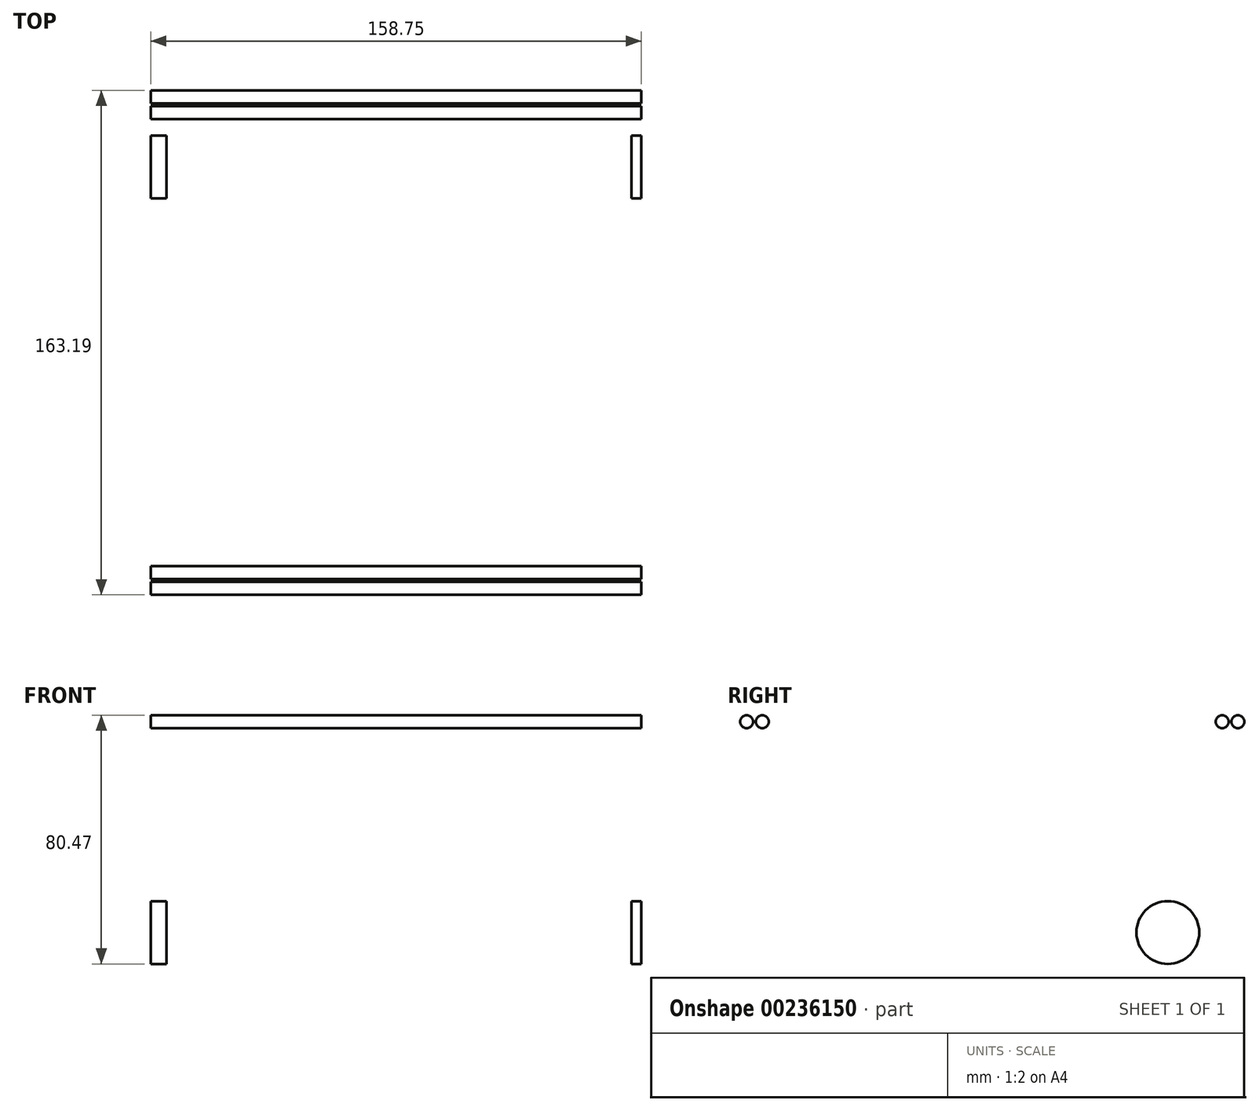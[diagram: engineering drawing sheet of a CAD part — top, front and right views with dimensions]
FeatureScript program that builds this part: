
annotation { "Feature Type Name" : "Feature", "Feature Type Description" : "" }
export const myFeature = defineFeature(function(context is Context, id is Id, definition is map)
    precondition{}
    {
        {
            var Q0;
            Q0=qCreatedBy(makeId("Top.planeOp"),FACE);
            var sketch = newSketch(context, id + "F0", { "sketchPlane" : qUnion([Q0])});
            skLineSegment(sketch, "E0.bottom", {"start": v(-87.64, 54.23) * mm, "end": v(71.1, 54.23) * mm});
            skLineSegment(sketch, "E0.top", {"start": v(-87.64, -104.78) * mm, "end": v(71.1, -104.78) * mm});
            skLineSegment(sketch, "E0.left", {"start": v(-87.64, 54.23) * mm, "end": v(-87.64, -104.78) * mm});
            skLineSegment(sketch, "E0.right", {"start": v(71.1, 54.23) * mm, "end": v(71.1, -104.78) * mm});
            skLineSegment(sketch, "E1.bottom", {"start": v(-94, 54.23) * mm, "end": v(-87.64, 54.23) * mm});
            skLineSegment(sketch, "E1.top", {"start": v(-94, 47.62) * mm, "end": v(-87.64, 47.62) * mm});
            skLineSegment(sketch, "E1.left", {"start": v(-94, 54.23) * mm, "end": v(-94, 47.63) * mm});
            skLineSegment(sketch, "E1.right", {"start": v(-87.64, 54.23) * mm, "end": v(-87.64, 47.63) * mm});
            skLineSegment(sketch, "E2", {"start": v(-91.77, 0) * mm, "end": v(128.93, 0) * mm, "construction": true});
            skLineSegment(sketch, "E3.bottom", {"start": v(-82.56, 49.15) * mm, "end": v(67.93, 49.15) * mm});
            skLineSegment(sketch, "E3.top", {"start": v(-82.56, -99.7) * mm, "end": v(67.93, -99.7) * mm});
            skLineSegment(sketch, "E3.left", {"start": v(-82.56, 49.15) * mm, "end": v(-82.56, -99.7) * mm});
            skLineSegment(sketch, "E3.right", {"start": v(67.93, 49.15) * mm, "end": v(67.93, -99.7) * mm});
            skLineSegment(sketch, "E4.0.1.0", {"start": v(-94, -3.18) * mm, "end": v(-87.64, -3.18) * mm});
            skLineSegment(sketch, "E4.0.1.1", {"start": v(-94, 3.43) * mm, "end": v(-94, -3.17) * mm});
            skLineSegment(sketch, "E4.0.1.2", {"start": v(-94, 3.43) * mm, "end": v(-87.64, 3.43) * mm});
            skLineSegment(sketch, "E4.0.2.0", {"start": v(-94, -53.98) * mm, "end": v(-87.64, -53.98) * mm});
            skLineSegment(sketch, "E4.0.2.1", {"start": v(-94, -47.37) * mm, "end": v(-94, -53.98) * mm});
            skLineSegment(sketch, "E4.0.2.2", {"start": v(-94, -47.37) * mm, "end": v(-87.64, -47.37) * mm});
            skLineSegment(sketch, "E4.0.3.0", {"start": v(-94, -104.78) * mm, "end": v(-87.64, -104.78) * mm});
            skLineSegment(sketch, "E4.0.3.1", {"start": v(-94, -98.17) * mm, "end": v(-94, -104.78) * mm});
            skLineSegment(sketch, "E4.0.3.2", {"start": v(-94, -98.17) * mm, "end": v(-87.64, -98.17) * mm});
            skLineSegment(sketch, "E4.direction1", {"start": v(-94, 47.63) * mm, "end": v(-68.6, 47.63) * mm, "construction": true});
            skLineSegment(sketch, "E4.direction2", {"start": v(-94, 47.63) * mm, "end": v(-94, -3.17) * mm, "construction": true});
            skSolve(sketch);
        }
        {
            var Q0;
            Q0=makeQuery(id+"F0.imprint","IMPRINT",FACE,{"disambiguationData":[TD([[makeQuery(id+"F0.imprint","IMPRINT",EDGE,{"derivedFrom":sQuery(id+"F0.wireOp",EDGE,"E0.bottom")}),-1.0]])]});
            var Q1;
            Q1=makeQuery(id+"F0.imprint","IMPRINT",FACE,{"disambiguationData":[TD([[makeQuery(id+"F0.imprint","IMPRINT",EDGE,{"derivedFrom":sQuery(id+"F0.wireOp",EDGE,"E1.bottom")}),-1.0]])]});
            var Q2;
            {var subQ0=sQuery(id+"F0.wireOp",EDGE,"E4.0.1.0");Q2=makeQuery(id+"F0.imprint","IMPRINT",FACE,{"disambiguationData":[TD([[makeQuery(id+"F0.imprint","IMPRINT",EDGE,{"derivedFrom":subQ0}),1.0]])]});}
            var Q3;
            {var subQ0=sQuery(id+"F0.wireOp",EDGE,"E4.0.2.0");Q3=makeQuery(id+"F0.imprint","IMPRINT",FACE,{"disambiguationData":[TD([[makeQuery(id+"F0.imprint","IMPRINT",EDGE,{"derivedFrom":subQ0}),1.0]])]});}
            var Q4;
            {var subQ0=sQuery(id+"F0.wireOp",EDGE,"E4.0.3.0");Q4=makeQuery(id+"F0.imprint","IMPRINT",FACE,{"disambiguationData":[TD([[makeQuery(id+"F0.imprint","IMPRINT",EDGE,{"derivedFrom":subQ0}),1.0]])]});}
            extrude(context, id + "F1", {"entities" : qUnion([Q0, Q1, Q2, Q3, Q4]), "depth" : 88.9 * mm});
        }
        {
            var Q0;
            {var subQ0=sQuery(id+"F0.wireOp",EDGE,"E0.left");Q0=makeQuery(id+"F1.opExtrude","SWEPT_FACE",FACE,{"disambiguationData":[OSD([subQ0]),TDD([makeQuery(id+"F0.imprint","IMPRINT",EDGE,{"disambiguationData":[TD([[makeQuery(id+"F0.imprint","INTERSECT",VERTEX,{"derivedFrom":[subQ0,sQuery(id+"F0.wireOp",EDGE,"E4.0.1.2")]}),1.0]])],"derivedFrom":subQ0})])]});}
            var sketch = newSketch(context, id + "F2", { "sketchPlane" : qUnion([Q0])});
            skCircle(sketch, "E5", {"center": v(-49.15, 86.8) * mm, "radius": 2.1 * mm});
            skCircle(sketch, "E6", {"center": v(99.7, 86.8) * mm, "radius": 2.1 * mm});
            skCircle(sketch, "E7", {"center": v(104.78, 86.8) * mm, "radius": 2.1 * mm});
            skCircle(sketch, "E8", {"center": v(-54.23, 86.8) * mm, "radius": 2.1 * mm});
            skSolve(sketch);
        }
        {
            var Q0;
            Q0=makeQuery(id+"F1.opExtrude","SWEPT_FACE",FACE,{"disambiguationData":[OSD([sQuery(id+"F0.wireOp",EDGE,"E0.right")])]});
            var sketch = newSketch(context, id + "F3", { "sketchPlane" : qUnion([Q0])});
            skCircle(sketch, "E9", {"center": v(-25.27, 88.9) * mm, "radius": 74.36 * mm});
            skPoint(sketch, "E9.first.point", {"position": v(-99.63, 88.9) * mm});
            skPoint(sketch, "E9.third.point", {"position": v(49.08, 88.9) * mm});
            skCircle(sketch, "E10", {"center": v(-82.12, 18.59) * mm, "radius": 10.16 * mm});
            skLineSegment(sketch, "E11", {"start": v(-25.27, 0) * mm, "end": v(-25.27, 125.52) * mm, "construction": true});
            skCircle(sketch, "E12.MirrorC", {"center": v(31.57, 18.59) * mm, "radius": 10.16 * mm});
            skSolve(sketch);
        }
        {
            var Q0;
            {var subQ0=sQuery(id+"F3.wireOp",EDGE,"E9");var subQ1=makeQuery(id+"F1.opExtrude","CAP_EDGE",EDGE,{"disambiguationData":[OSD([sQuery(id+"F0.wireOp",EDGE,"E0.right")])],"isStart":false});var subQ2=makeQuery(id+"F3.imprint","INTERSECT",VERTEX,{"disambiguationData":[OD(0.0)],"derivedFrom":[subQ1,subQ0]});Q0=makeQuery(id+"F3.imprint","IMPRINT",FACE,{"disambiguationData":[TD([[makeQuery(id+"F3.imprint","IMPRINT",EDGE,{"disambiguationData":[TD([[subQ2,1.0]])],"derivedFrom":subQ0}),1.0]])]});}
            var Q1;
            Q1=makeQuery(id+"F3.imprint","IMPRINT",FACE,{"disambiguationData":[TD([[makeQuery(id+"F3.imprint","IMPRINT",EDGE,{"derivedFrom":sQuery(id+"F3.wireOp",EDGE,"E10")}),1.0]])]});
            var Q2;
            Q2=makeQuery(id+"F3.imprint","IMPRINT",FACE,{"disambiguationData":[TD([[makeQuery(id+"F3.imprint","IMPRINT",EDGE,{"derivedFrom":sQuery(id+"F3.wireOp",EDGE,"E12.MirrorC")}),-1.0]])]});
            extrude(context, id + "F4", {"entities" : qUnion([Q0, Q1, Q2]), "operationType" : NewBodyOperationType.REMOVE, "oppositeDirection" : true, "depth" : 187.7 * mm});
        }
        {
            var Q0;
            Q0=makeQuery(id+"F2.imprint","IMPRINT",FACE,{"disambiguationData":[TD([[makeQuery(id+"F2.imprint","IMPRINT",EDGE,{"derivedFrom":sQuery(id+"F2.wireOp",EDGE,"E7")}),1.0]])]});
            var Q1;
            Q1=makeQuery(id+"F2.imprint","IMPRINT",FACE,{"disambiguationData":[TD([[makeQuery(id+"F2.imprint","IMPRINT",EDGE,{"derivedFrom":sQuery(id+"F2.wireOp",EDGE,"E8")}),1.0]])]});
            var Q2;
            {var subQ0=sQuery(id+"F2.wireOp",EDGE,"E5");var subQ1=makeQuery(id+"F1.opExtrude","SWEPT_EDGE",EDGE,{"disambiguationData":[OSD([sQuery(id+"F0.wireOp",EDGE,"E0.left"),sQuery(id+"F0.wireOp",EDGE,"E1.top"),sQuery(id+"F0.wireOp",EDGE,"E1.right")])]});var subQ2=makeQuery(id+"F2.imprint","INTERSECT",VERTEX,{"disambiguationData":[OD(0.0)],"derivedFrom":[subQ1,subQ0]});Q2=makeQuery(id+"F2.imprint","IMPRINT",FACE,{"disambiguationData":[TD([[makeQuery(id+"F2.imprint","IMPRINT",EDGE,{"disambiguationData":[TD([[subQ2,1.0]])],"derivedFrom":subQ0}),1.0]])]});}
            var Q3;
            {var subQ0=sQuery(id+"F2.wireOp",EDGE,"E5");var subQ1=makeQuery(id+"F1.opExtrude","SWEPT_EDGE",EDGE,{"disambiguationData":[OSD([sQuery(id+"F0.wireOp",EDGE,"E0.left"),sQuery(id+"F0.wireOp",EDGE,"E1.top"),sQuery(id+"F0.wireOp",EDGE,"E1.right")])]});var subQ2=makeQuery(id+"F2.imprint","INTERSECT",VERTEX,{"disambiguationData":[OD(0.0)],"derivedFrom":[subQ1,subQ0]});Q3=makeQuery(id+"F2.imprint","IMPRINT",FACE,{"disambiguationData":[TD([[makeQuery(id+"F2.imprint","IMPRINT",EDGE,{"disambiguationData":[TD([[subQ2,-1.0]])],"derivedFrom":subQ0}),1.0]])]});}
            var Q4;
            Q4=makeQuery(id+"F2.imprint","IMPRINT",FACE,{"disambiguationData":[TD([[makeQuery(id+"F2.imprint","IMPRINT",EDGE,{"derivedFrom":sQuery(id+"F2.wireOp",EDGE,"E6")}),1.0]])]});
            var Q5;
            Q5=makeQuery(id+"F1.opExtrude","SWEPT_FACE",FACE,{"disambiguationData":[OSD([sQuery(id+"F0.wireOp",EDGE,"E0.right")])]});
            extrude(context, id + "F5", {"entities" : qUnion([Q0, Q1, Q2, Q3, Q4]), "operationType" : NewBodyOperationType.ADD, "endBound" : BoundingType.UP_TO_SURFACE, "oppositeDirection" : true, "endBoundEntityFace" : qUnion([Q5]), "depth" : 143 * mm});
        }
    });
